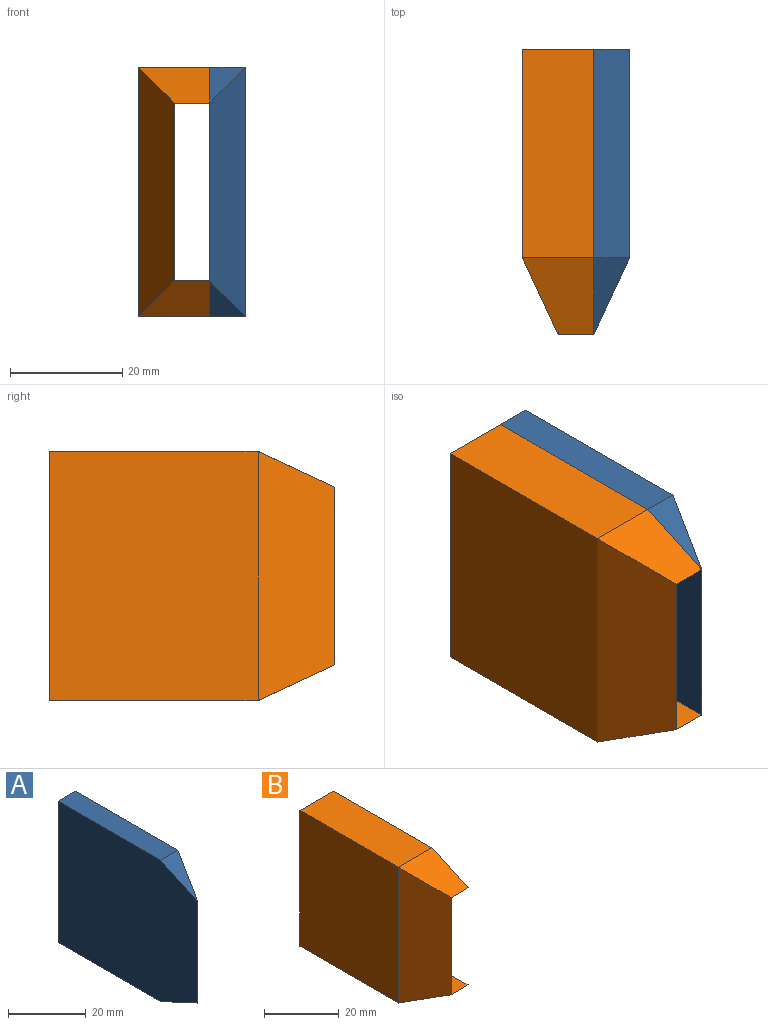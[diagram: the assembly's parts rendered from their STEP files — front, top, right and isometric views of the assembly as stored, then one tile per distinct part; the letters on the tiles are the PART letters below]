
ASSEMBLY  parts=2 mates=1
PART A: 8 faces, bbox 6.4x50.8x44.5 mm
  f0: plane 37.18x6.35mm, normal (0,0,-1), area 236.1mm2, adj f1,f3,f4,f7
  f1: plane 44.45x37.18mm, normal (1,0,0), area 1652.8mm2, adj f0,f2,f4,f6
  f2: plane 37.18x6.35mm, normal (0,0,1), area 236.1mm2, adj f1,f3,f4,f5
  f3: plane 50.8x44.45mm, normal (-1,0,0), area 2171.6mm2, adj f0,f2,f4,f5,f6,f7
  f4: plane 44.45x6.35mm, normal (0,1,0), area 282.3mm2, adj f0,f1,f2,f3
  f5: plane 13.62x6.35mm, normal (0,-0.42,0.91), area 47.7mm2, adj f2,f3,f6
  f6: plane 44.45x13.62mm, normal (0.91,-0.42,0), area 572.5mm2, adj f1,f3,f5,f7
  f7: plane 13.62x6.35mm, normal (0,-0.42,-0.91), area 47.7mm2, adj f0,f3,f6
PART B: 13 faces, bbox 12.7x50.8x44.5 mm
  f0: plane 50.8x6.35mm, normal (1,0,0), area 279.3mm2, adj f1,f7,f9,f12
  f1: plane 37.18x12.7mm, normal (0,0,1), area 472.2mm2, adj f0,f2,f9,f12
  f2: plane 44.45x37.21mm, normal (-1,0,0), area 1654mm2, adj f1,f3,f9,f10,f11,f12
  f3: plane 37.18x12.7mm, normal (0,0,-1), area 472.2mm2, adj f2,f4,f9,f11
  f4: plane 50.8x6.35mm, normal (1,0,0), area 279.3mm2, adj f3,f5,f9,f11
  f5: plane 50.8x6.35mm, normal (0,0,1), area 322.6mm2, adj f4,f6,f9,f11
  f6: plane 50.8x31.75mm, normal (1,0,0), area 1612.9mm2, adj f5,f7,f8,f9
  f7: plane 50.8x6.35mm, normal (0,0,-1), area 322.6mm2, adj f0,f6,f9,f12
  f8: plane 31.75x0.01mm, normal (0,-1,0), area 0.4mm2, adj f6,f10,f11,f12
  f9: plane 44.45x12.7mm, normal (0,1,0), area 362.9mm2, adj f0,f1,f2,f3,f4,f5,f6,f7
  f10: plane 44.42x13.59mm, normal (-0.91,-0.42,0), area 571.1mm2, adj f2,f8,f11,f12
  f11: plane 13.62x12.7mm, normal (0,-0.42,-0.91), area 143.3mm2, adj f2,f3,f4,f5,f8,f10
  f12: plane 13.62x12.7mm, normal (0,-0.42,0.91), area 143.3mm2, adj f0,f1,f2,f7,f8,f10
PLACE A t=(-22.31,-14.45,-8.13)mm
PLACE B t=(-55.27,-14.45,-8.13)mm
MATE fastened A.f4 <-> B.f9  axis (0,1,0) through (-35.62,-14.45,-8.13)mm
